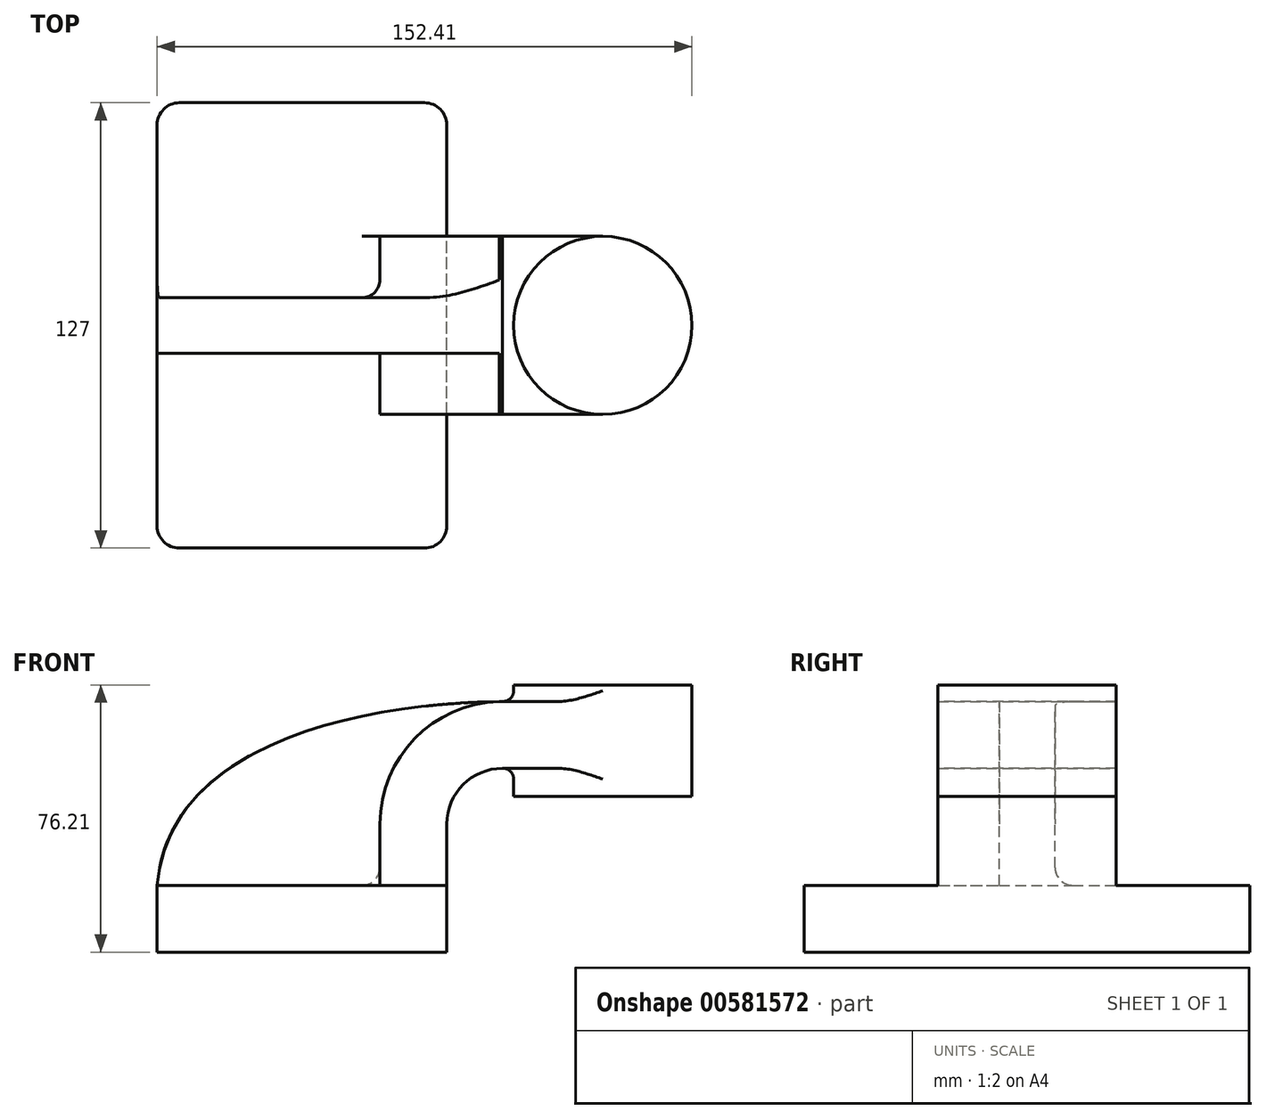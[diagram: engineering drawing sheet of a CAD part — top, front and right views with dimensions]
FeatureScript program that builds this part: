
annotation { "Feature Type Name" : "Feature", "Feature Type Description" : "" }
export const myFeature = defineFeature(function(context is Context, id is Id, definition is map)
    precondition{}
    {
        {
            var Q0;
            Q0=qCreatedBy(makeId("Front.planeOp"),FACE);
            var sketch = newSketch(context, id + "F0", { "sketchPlane" : qUnion([Q0])});
            skLineSegment(sketch, "E0.bottom", {"start": v(-41.28, 9.53) * mm, "end": v(41.28, 9.53) * mm});
            skLineSegment(sketch, "E0.top", {"start": v(-41.28, -9.53) * mm, "end": v(41.28, -9.53) * mm});
            skLineSegment(sketch, "E0.left", {"start": v(-41.28, 9.53) * mm, "end": v(-41.28, -9.52) * mm});
            skLineSegment(sketch, "E0.right", {"start": v(41.28, 9.53) * mm, "end": v(41.28, -9.53) * mm});
            skLineSegment(sketch, "E1", {"start": v(41.27, 9.53) * mm, "end": v(41.27, 27) * mm});
            skArc(sketch, "E2", {"start": v(41.28, 27) * mm, "mid": v(45.92, 38.23) * mm, "end": v(57.15, 42.88) * mm});
            skLineSegment(sketch, "E3", {"start": v(57.15, 42.88) * mm, "end": v(85.72, 42.88) * mm});
            skLineSegment(sketch, "E4.bottom", {"start": v(111.12, 66.68) * mm, "end": v(60.33, 66.68) * mm});
            skLineSegment(sketch, "E4.top", {"start": v(111.12, 34.93) * mm, "end": v(60.33, 34.93) * mm});
            skLineSegment(sketch, "E4.left", {"start": v(111.12, 66.68) * mm, "end": v(111.12, 34.93) * mm});
            skLineSegment(sketch, "E4.right", {"start": v(60.33, 66.68) * mm, "end": v(60.33, 34.93) * mm});
            skPoint(sketch, "E4.middle", {"position": v(85.72, 50.8) * mm});
            skLineSegment(sketch, "E5.0", {"start": v(57.15, 61.93) * mm, "end": v(85.72, 61.93) * mm});
            skArc(sketch, "E5.1", {"start": v(22.23, 27) * mm, "mid": v(32.45, 51.7) * mm, "end": v(57.15, 61.93) * mm});
            skLineSegment(sketch, "E5.2", {"start": v(22.23, 9.53) * mm, "end": v(22.23, 27) * mm});
            skLineSegment(sketch, "E6", {"start": v(85.72, 66.68) * mm, "end": v(85.72, 34.93) * mm});
            skFitSpline(sketch, "E7", {"points": [v(-41.28, 9.52) * mm, v(57.15, 61.93) * mm], "startDerivative": vector(10.1, 120.96) * mm, "endDerivative": vector(123.13, 1.43) * mm});
            skSolve(sketch);
        }
        {
            var Q0;
            Q0=makeQuery(id+"F0.imprint","IMPRINT",FACE,{"disambiguationData":[TD([[makeQuery(id+"F0.imprint","IMPRINT",EDGE,{"derivedFrom":sQuery(id+"F0.wireOp",EDGE,"E0.top")}),1.0]])]});
            extrude(context, id + "F1", {"entities" : qUnion([Q0]), "endBound" : BoundingType.SYMMETRIC, "depth" : 127 * mm, "offsetDistance" : 25.4 * mm});
        }
        {
            var Q0;
            {var subQ4=sQuery(id+"F0.wireOp",EDGE,"E1");Q0=makeQuery(id+"F0.imprint","IMPRINT",FACE,{"disambiguationData":[TD([[makeQuery(id+"F0.imprint","IMPRINT",EDGE,{"derivedFrom":subQ4}),1.0]])]});}
            var Q1;
            {var subQ0=sQuery(id+"F0.wireOp",EDGE,"E6");var subQ1=sQuery(id+"F0.wireOp",EDGE,"E3");var subQ2=makeQuery(id+"F0.imprint","INTERSECT",VERTEX,{"derivedFrom":[subQ1,subQ0]});Q1=makeQuery(id+"F0.imprint","IMPRINT",FACE,{"disambiguationData":[TD([[makeQuery(id+"F0.imprint","IMPRINT",EDGE,{"disambiguationData":[TD([[subQ2,1.0]])],"derivedFrom":subQ1}),1.0]])]});}
            extrude(context, id + "F2", {"entities" : qUnion([Q0, Q1]), "operationType" : NewBodyOperationType.ADD, "endBound" : BoundingType.SYMMETRIC, "depth" : 50.8 * mm, "offsetDistance" : 25.4 * mm});
        }
        {
            var Q0;
            {var subQ3=sQuery(id+"F0.wireOp",EDGE,"E5.2");Q0=makeQuery(id+"F0.imprint","IMPRINT",FACE,{"disambiguationData":[TD([[makeQuery(id+"F0.imprint","IMPRINT",EDGE,{"derivedFrom":subQ3}),1.0]])]});}
            extrude(context, id + "F3", {"entities" : qUnion([Q0]), "operationType" : NewBodyOperationType.ADD, "endBound" : BoundingType.SYMMETRIC, "depth" : 15.88 * mm, "offsetDistance" : 25.4 * mm});
        }
        {
            var Q0;
            {var subQ4=sQuery(id+"F0.wireOp",EDGE,"E4.left");Q0=makeQuery(id+"F0.imprint","IMPRINT",FACE,{"disambiguationData":[TD([[makeQuery(id+"F0.imprint","IMPRINT",EDGE,{"derivedFrom":subQ4}),-1.0]])]});}
            var Q1;
            Q1=sQuery(id+"F0.wireOp",EDGE,"E6");
            revolve(context, id + "F4", {"operationType" : NewBodyOperationType.ADD, "entities" : qUnion([Q0]), "axis" : qUnion([Q1]), "revolveType" : RevolveType.FULL});
        }
        {
            var Q0;
            Q0=makeQuery(id+"F1.opExtrude","CAP_EDGE",EDGE,{"disambiguationData":[OSD([sQuery(id+"F0.wireOp",EDGE,"E0.right")])],"isStart":false});
            var Q1;
            Q1=makeQuery(id+"F1.opExtrude","CAP_EDGE",EDGE,{"disambiguationData":[OSD([sQuery(id+"F0.wireOp",EDGE,"E0.left")])],"isStart":false});
            var Q2;
            Q2=makeQuery(id+"F1.opExtrude","CAP_EDGE",EDGE,{"disambiguationData":[OSD([sQuery(id+"F0.wireOp",EDGE,"E0.right")])],"isStart":true});
            var Q3;
            Q3=makeQuery(id+"F1.opExtrude","CAP_EDGE",EDGE,{"disambiguationData":[OSD([sQuery(id+"F0.wireOp",EDGE,"E0.left")])],"isStart":true});
            fillet(context, id + "F5", {"entities" : qUnion([Q0, Q1, Q2, Q3]), "radius" : 6.35 * mm, "tangentPropagation" : true, "allowEdgeOverflow" : false});
        }
        {
            var Q0;
            Q0=makeQuery(id+"F4.boolean.opBoolean","INTERSECT",EDGE,{"derivedFrom":[makeQuery(id+"F2.opExtrude","SWEPT_FACE",FACE,{"disambiguationData":[OSD([sQuery(id+"F0.wireOp",EDGE,"E5.0")])]}),makeQuery(id+"F4.opRevolve","SWEPT_FACE",FACE,{"disambiguationData":[OSD([sQuery(id+"F0.wireOp",EDGE,"E4.left")])]})]});
            var Q1;
            Q1=makeQuery(id+"F4.boolean.opBoolean","INTERSECT",EDGE,{"derivedFrom":[makeQuery(id+"F2.opExtrude","SWEPT_FACE",FACE,{"disambiguationData":[OSD([sQuery(id+"F0.wireOp",EDGE,"E3")])]}),makeQuery(id+"F4.opRevolve","SWEPT_FACE",FACE,{"disambiguationData":[OSD([sQuery(id+"F0.wireOp",EDGE,"E4.left")])]})]});
            fillet(context, id + "F6", {"entities" : qUnion([Q0, Q1]), "radius" : 3.07 * mm, "tangentPropagation" : true, "allowEdgeOverflow" : false});
        }
        {
            var Q0;
            Q0=makeQuery(id+"F3.opExtrude","CAP_EDGE",EDGE,{"disambiguationData":[OSD([sQuery(id+"F0.wireOp",EDGE,"E0.bottom")])],"isStart":false});
            var Q1;
            Q1=makeQuery(id+"F3.opExtrude","CAP_EDGE",EDGE,{"disambiguationData":[OSD([sQuery(id+"F0.wireOp",EDGE,"E0.bottom")])],"isStart":true});
            fillet(context, id + "F7", {"entities" : qUnion([Q0, Q1]), "radius" : 5.08 * mm, "tangentPropagation" : true, "allowEdgeOverflow" : false});
        }
        {
            var Q0;
            Q0=makeQuery(id+"F3.opExtrude","CAP_EDGE",EDGE,{"disambiguationData":[OSD([sQuery(id+"F0.wireOp",EDGE,"E5.1")])],"isStart":true});
            var Q1;
            Q1=makeQuery(id+"F3.opExtrude","CAP_EDGE",EDGE,{"disambiguationData":[OSD([sQuery(id+"F0.wireOp",EDGE,"E5.1")])],"isStart":false});
            fillet(context, id + "F8", {"entities" : qUnion([Q0, Q1]), "radius" : 5.08 * mm, "tangentPropagation" : true, "allowEdgeOverflow" : false});
        }
    });
